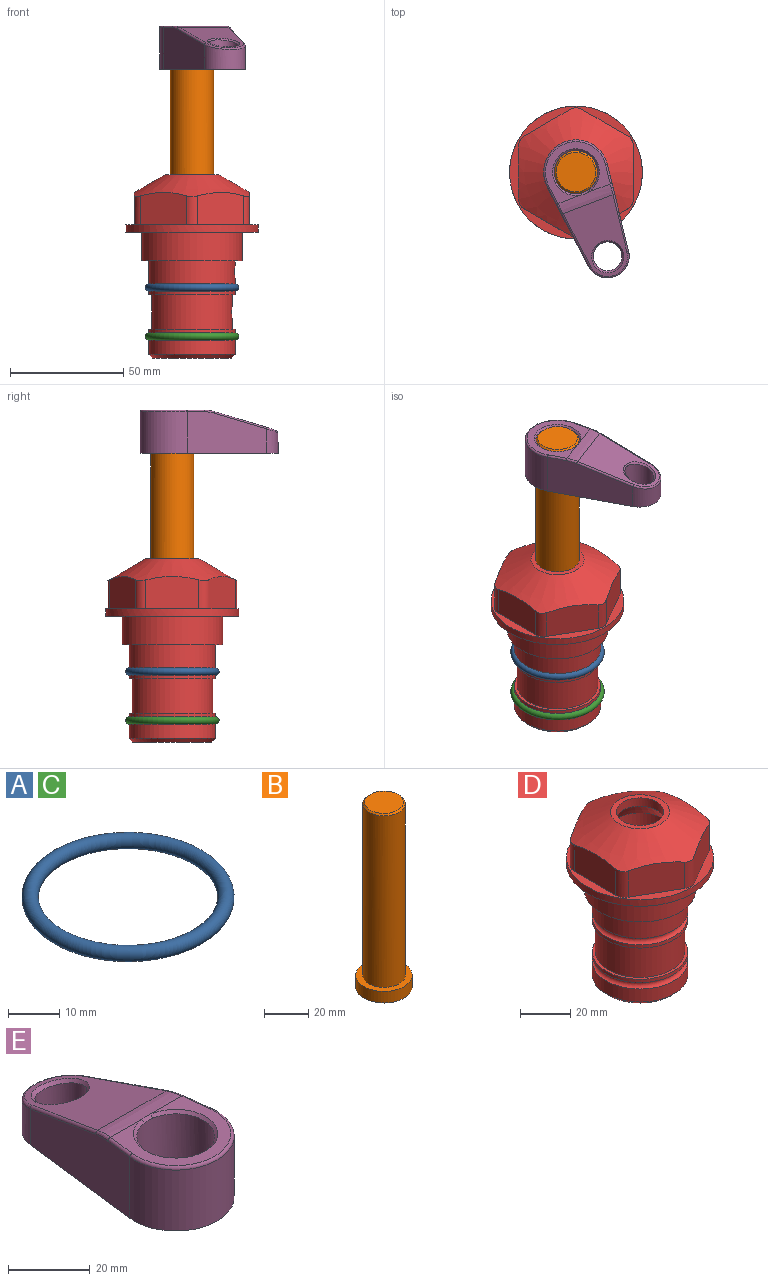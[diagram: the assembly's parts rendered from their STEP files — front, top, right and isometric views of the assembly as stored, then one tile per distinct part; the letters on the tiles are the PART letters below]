
ASSEMBLY  parts=5 mates=4
PART A: 1 faces, bbox 44.7x44.7x3.2 mm
  f0: torus R=19.05mm, axis (0,0,1), area 1193.9mm2
PART B: 6 faces, bbox 25.4x25.4x101.6 mm
  f0: plane 17.46x17.46mm, normal (0,0,1), area 239.5mm2, adj f5
  f1: plane 25.4x25.4mm, normal (0,0,-1), area 506.7mm2, adj f2
  f2: cylinder r=12.7mm len=25.4mm, axis (0,0,1), area 506.7mm2, adj f1,f3
  f3: plane 25.4x25.4mm, normal (0,0,1), area 221.7mm2, adj f2,f4
  f4: cylinder r=9.53mm len=94.46mm, axis (0,0,1), area 5653mm2, adj f3,f5
  f5: cone r=8.73mm half-angle=45deg, axis (0,0,-1), area 64.4mm2, adj f0,f4
PART C: same geometry as A
PART D: 36 faces, bbox 58.7x58.7x81 mm
  f0: cylinder r=17.78mm len=35.56mm, axis (0,0,1), area 1670.8mm2, adj f23,f24,f31
  f1: cylinder r=19.05mm len=38.1mm, axis (0,0,1), area 1191.9mm2, adj f26,f27,f30
  f2: plane 58.66x58.66mm, normal (0,0,-1), area 1150.6mm2, adj f3,f28
  f3: cylinder r=29.33mm len=58.66mm, axis (0,0,-1), area 585.1mm2, adj f2,f4
  f4: plane 58.66x58.66mm, normal (0,0,1), area 475.9mm2, adj f3,f5,f6,f7,f8,f9,f10,f11
  f5: plane 20.32x14.34mm, normal (-0.5,0.87,0), area 324.4mm2, adj f4,f15,f16,f17
  f6: plane 20.32x14.34mm, normal (0.5,0.87,0), area 324.4mm2, adj f4,f14,f15,f17
  f7: plane 23.48x14.34mm, normal (1,0,0), area 324.4mm2, adj f4,f13,f14,f17
  f8: plane 20.32x14.34mm, normal (0.5,-0.87,0), area 324.4mm2, adj f4,f12,f13,f17
  f9: plane 20.32x14.34mm, normal (-0.5,-0.87,0), area 324.4mm2, adj f4,f11,f12,f17
  f10: plane 23.48x14.34mm, normal (-1,0,0), area 324.4mm2, adj f4,f11,f16,f17
  f11: cylinder r=5.08mm len=12.85mm, axis (0,0,-1), area 67.2mm2, adj f4,f9,f10,f17
  f12: cylinder r=5.08mm len=12.85mm, axis (0,0,-1), area 67.2mm2, adj f4,f8,f9,f17
  f13: cylinder r=5.08mm len=12.85mm, axis (0,0,-1), area 67.2mm2, adj f4,f7,f8,f17
  f14: cylinder r=5.08mm len=12.85mm, axis (0,0,-1), area 67.2mm2, adj f4,f6,f7,f17
  f15: cylinder r=5.08mm len=12.85mm, axis (0,0,-1), area 67.2mm2, adj f4,f5,f6,f17
  f16: cylinder r=5.08mm len=12.85mm, axis (0,0,-1), area 67.2mm2, adj f4,f5,f10,f17
  f17: cone r=11.73mm half-angle=60deg, axis (0,0,-1), area 2071.8mm2, adj f5,f6,f7,f8,f9,f10,f11,f12
  f18: plane 23.46x23.46mm, normal (0,0,1), area 147.4mm2, adj f17,f35
  f19: plane 34.93x34.93mm, normal (0,0,-1), area 958mm2, adj f29
  f20: cylinder r=19.05mm len=38.1mm, axis (0,0,1), area 760.1mm2, adj f21,f29
  f21: torus R=19.05mm, axis (0,0,1), area 565.3mm2, adj f20,f22
  f22: cylinder r=19.05mm len=38.1mm, axis (0,0,1), area 190mm2, adj f21,f23
  f23: plane 38.1x38.1mm, normal (0,0,1), area 146.9mm2, adj f0,f22
  f24: plane 38.1x38.1mm, normal (0,0,-1), area 146.9mm2, adj f0,f25
  f25: cylinder r=19.05mm len=38.1mm, axis (0,0,1), area 190mm2, adj f24,f26
  f26: torus R=19.05mm, axis (0,0,1), area 565.3mm2, adj f1,f25
  f27: plane 44.45x44.45mm, normal (0,0,-1), area 411.7mm2, adj f1,f28
  f28: cylinder r=22.23mm len=44.45mm, axis (0,0,1), area 1773.5mm2, adj f2,f27
  f29: cone r=19.05mm half-angle=45deg, axis (0,0,1), area 257.5mm2, adj f19,f20
  f30: cylinder r=3.17mm len=6.75mm, axis (-1,0,0), area 128mm2, adj f1,f33
  f31: cylinder r=3.17mm len=6.35mm, axis (-1,0,0), area 102.5mm2, adj f0,f33
  f32: plane 25.4x25.4mm, normal (0,0,1), area 506.7mm2, adj f33
  f33: cylinder r=12.7mm len=66.42mm, axis (0,0,-1), area 5236.2mm2, adj f30,f31,f32,f34
  f34: cone r=9.53mm half-angle=30deg, axis (0,0,-1), area 443.4mm2, adj f33,f35
  f35: cylinder r=9.53mm len=19.05mm, axis (0,0,-1), area 240.9mm2, adj f18,f34
PART E: 31 faces, bbox 31.7x65.5x19.8 mm
  f0: plane 39.12x18.26mm, normal (0.99,0.12,0), area 612.2mm2, adj f1,f4,f7,f11,f13,f15
  f1: cylinder r=9.53mm len=18.91mm, axis (0,0,-1), area 296.1mm2, adj f0,f2,f7,f17
  f2: plane 39.12x18.26mm, normal (-0.99,0.12,0), area 612.2mm2, adj f1,f4,f7,f12,f14,f16
  f3: cylinder r=6.35mm len=12.7mm, axis (0,0,-1), area 362.4mm2, adj f7,f18
  f4: cylinder r=14.29mm len=28.58mm, axis (0,0,-1), area 882.2mm2, adj f0,f2,f7,f10
  f5: cylinder r=9.53mm len=19.05mm, axis (0,0,-1), area 1092.6mm2, adj f7,f19,f20
  f6: plane 26.99x23.69mm, normal (0,0,1), area 216.2mm2, adj f9,f10,f11,f12,f19
  f7: plane 63.5x28.58mm, normal (0,0,-1), area 661.8mm2, adj f0,f1,f2,f3,f4,f5,f22,f23
  f8: plane 33.52x23.6mm, normal (0,0.26,0.97), area 486mm2, adj f9,f15,f16,f17,f18
  f9: cylinder r=19.05mm len=24.72mm, axis (1,0,0), area 120.4mm2, adj f6,f8,f13,f14,f20
  f10: torus R=13.49mm, axis (0,0,1), area 59mm2, adj f4,f6,f11,f12
  f11: cylinder r=0.79mm len=8.67mm, axis (0.12,-0.99,0), area 10.8mm2, adj f0,f6,f10,f13
  f12: cylinder r=0.79mm len=8.67mm, axis (0.12,0.99,0), area 10.8mm2, adj f2,f6,f10,f14
  f13: bspline ~4.95x1.42mm, area 6.1mm2, adj f0,f9,f11,f15
  f14: bspline ~4.95x1.42mm, area 6.1mm2, adj f2,f9,f12,f16
  f15: cylinder r=0.79mm len=25.95mm, axis (0.12,-0.96,0.26), area 32.9mm2, adj f0,f8,f13,f17
  f16: cylinder r=0.79mm len=25.95mm, axis (0.12,0.96,-0.26), area 32.9mm2, adj f2,f8,f14,f17
  f17: bspline ~18.91x8.38mm, area 30mm2, adj f1,f8,f15,f16
  f18: bspline ~14.29x14.29mm, area 48.3mm2, adj f3,f8
  f19: cone r=9.53mm half-angle=45deg, axis (0,0,1), area 66.5mm2, adj f5,f6,f20
  f20: bspline ~3.22x0.96mm, area 3.5mm2, adj f5,f9,f19
  f21: plane 2.75x2.72mm, normal (0,0,-1), area 2.9mm2, adj f23,f25,f28
  f22: plane 23.05x15.88mm, normal (-0.99,-0.12,0), area 323.6mm2, adj f7,f25,f26,f27,f28,f29
  f23: plane 23.05x15.88mm, normal (0.99,-0.12,0), area 323.6mm2, adj f7,f21,f25,f27,f28,f30
  f24: cylinder r=9.53mm len=10.69mm, axis (0,0,-1), area 114.7mm2, adj f7,f27,f29,f30
  f25: cylinder r=12.7mm len=20.59mm, axis (0,0,-1), area 381.1mm2, adj f7,f21,f22,f23,f26,f28
  f26: plane 2.75x2.72mm, normal (0,0,-1), area 2.9mm2, adj f22,f25,f28
  f27: plane 19.72x18.37mm, normal (0,-0.26,-0.97), area 291.8mm2, adj f22,f23,f24,f28,f29,f30
  f28: cylinder r=15.88mm len=19.92mm, axis (1,0,0), area 54.8mm2, adj f21,f22,f23,f25,f26,f27
  f29: cylinder r=1.59mm len=11mm, axis (0,0,-1), area 34.7mm2, adj f7,f22,f24,f27
  f30: cylinder r=1.59mm len=11mm, axis (0,0,-1), area 34.7mm2, adj f7,f23,f24,f27
PLACE A at identity
PLACE B rot(axis=(0,0,-1),159.4deg) t=(0,0,27.55)mm
PLACE C t=(0,0,-21.59)mm
PLACE D at identity fixed
PLACE E rot(axis=(0,0,-1),159.4deg) t=(0,0,27.55)mm
MATE fastened A.f0 <-> D.f0  axis (0,0,1) through (0,0,-24.51)mm
MATE cylindrical B.f2 <-> D.f0  axis (0,0,-1) through (0,0,-10.55)mm
MATE fastened B.f2 <-> E.f4  axis (0,0,1) through (0,0,90.26)mm
MATE fastened C.f0 <-> D.f0  axis (0,0,1) through (0,0,-46.1)mm
